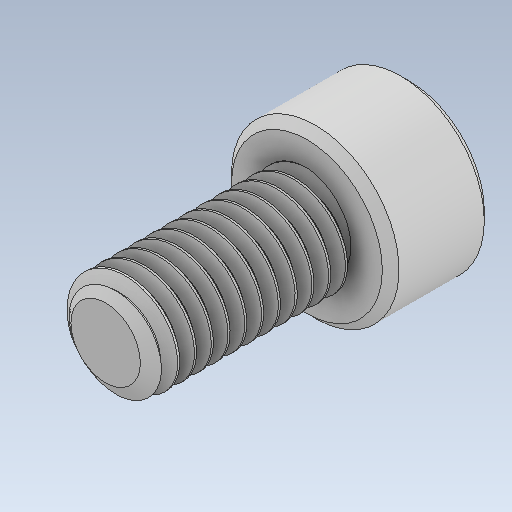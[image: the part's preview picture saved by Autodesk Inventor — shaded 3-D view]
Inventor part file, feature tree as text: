
AUTODESK INVENTOR PART (.ipt)
format: ipt  version: 2023 (Build 270158000, 158)  size: 529,408 bytes
history: native  units: in
note: dims shown in document units (in); Inventor stores cm internally (conversion verified against a paired STEP export)
features: chamfer x1
ambient origin geometry x8: Origin, YZ Plane, XZ Plane, XY Plane, X Axis, Y Axis, Z Axis, Center Point
bodies: Solid1 (feature_tree)
feature tree (1):
  chamfer  "Chamfer1"  [1 undecoded]
note: 1 required parameter value undecoded (feature->parameter linkage not recoverable at this tier; creation-order binding heuristic only, values carry confidence <= 0.55)
